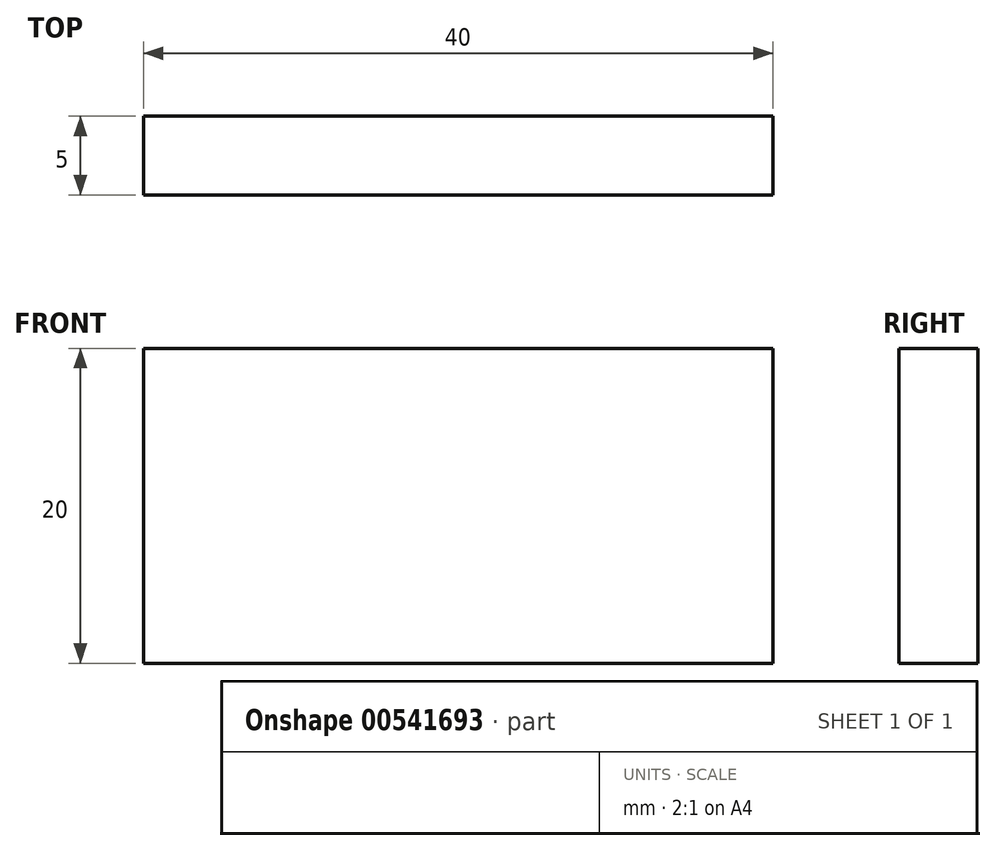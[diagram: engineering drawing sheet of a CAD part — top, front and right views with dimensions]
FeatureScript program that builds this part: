
annotation { "Feature Type Name" : "Feature", "Feature Type Description" : "" }
export const myFeature = defineFeature(function(context is Context, id is Id, definition is map)
    precondition{}
    {
        {
            var Q0;
            Q0=qCreatedBy(makeId("Front.planeOp"),FACE);
            var sketch = newSketch(context, id + "F0", { "sketchPlane" : qUnion([Q0])});
            skPoint(sketch, "E0.middle", {"position": v(0, 0) * mm});
            skPoint(sketch, "E1.middle", {"position": v(0, 12.39) * mm});
            skPoint(sketch, "E1.middle.positionSnap0", {"position": v(0, 17.3) * mm});
            skPoint(sketch, "E1.centerSnap0", {"position": v(0, 17.3) * mm});
            skLineSegment(sketch, "E2.bottom", {"start": v(20, -10) * mm, "end": v(-20, -10) * mm});
            skLineSegment(sketch, "E2.top", {"start": v(20, 10) * mm, "end": v(-20, 10) * mm});
            skLineSegment(sketch, "E2.left", {"start": v(20, -10) * mm, "end": v(20, 10) * mm});
            skLineSegment(sketch, "E2.right", {"start": v(-20, -10) * mm, "end": v(-20, 10) * mm});
            skSolve(sketch);
        }
        {
            var Q0;
            Q0 = qSketchRegion(id + "F0", true);
            extrude(context, id + "F1", {"entities" : qUnion([Q0]), "depth" : 5 * mm, "offsetDistance" : 25.4 * mm});
        }
    });
